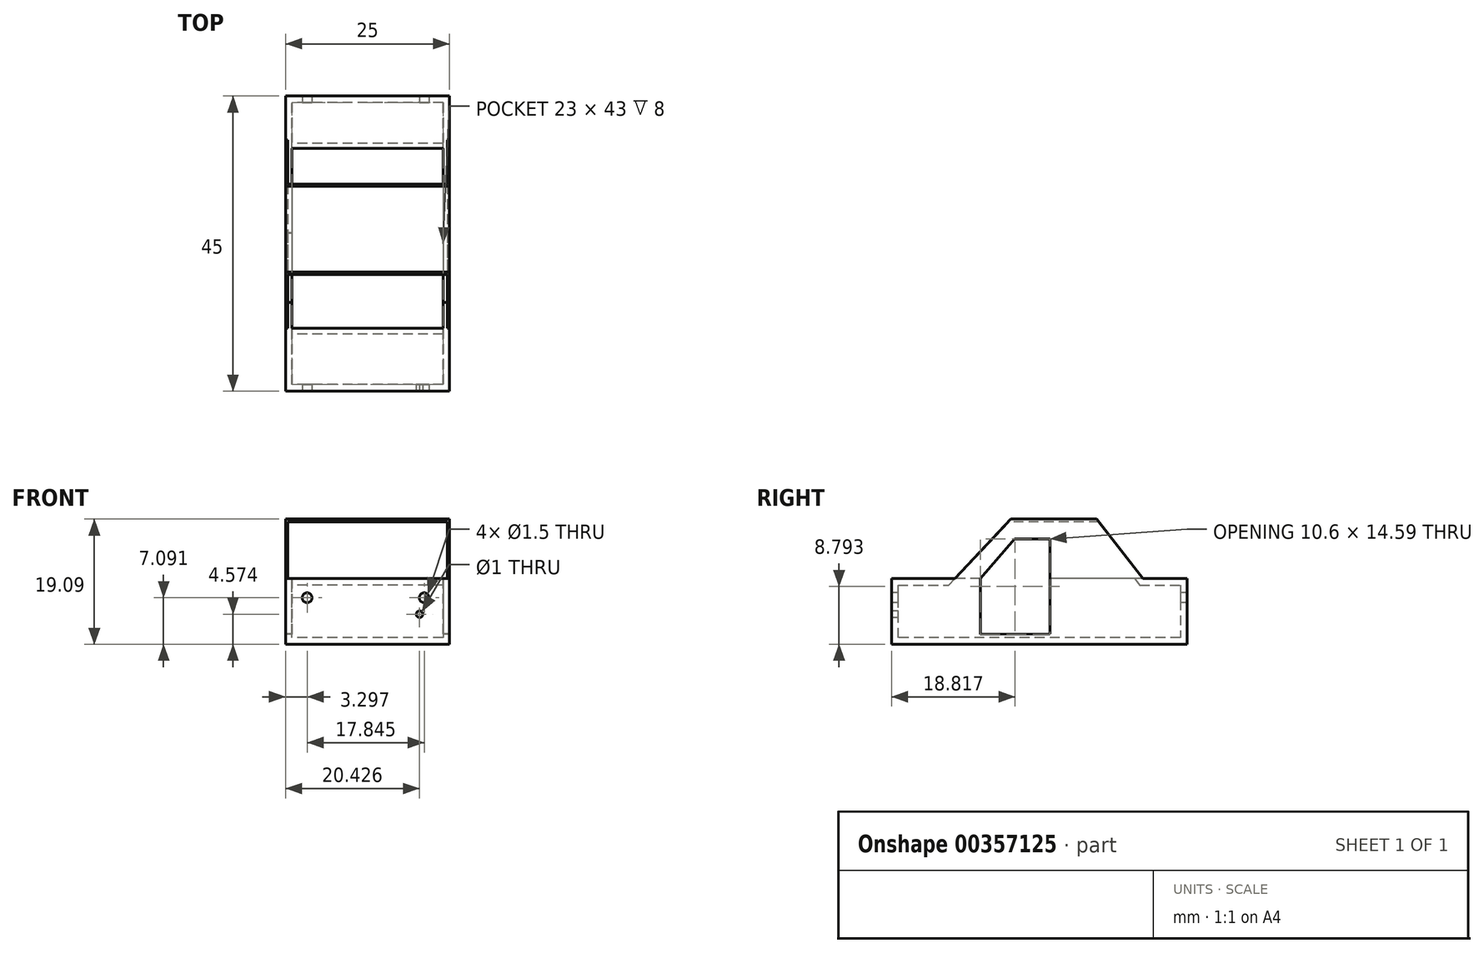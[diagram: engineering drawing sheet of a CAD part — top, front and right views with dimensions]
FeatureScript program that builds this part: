
annotation { "Feature Type Name" : "Feature", "Feature Type Description" : "" }
export const myFeature = defineFeature(function(context is Context, id is Id, definition is map)
    precondition{}
    {
        {
            var Q0;
            Q0=qCreatedBy(makeId("Right.planeOp"),FACE);
            var sketch = newSketch(context, id + "F0", { "sketchPlane" : qUnion([Q0])});
            skLineSegment(sketch, "E0", {"start": v(0, 0) * mm, "end": v(9.63, 0) * mm});
            skLineSegment(sketch, "E1", {"start": v(9.63, 0) * mm, "end": v(18.17, 9.09) * mm});
            skLineSegment(sketch, "E2", {"start": v(18.17, 9.09) * mm, "end": v(31.26, 9.09) * mm});
            skLineSegment(sketch, "E3", {"start": v(31.26, 9.09) * mm, "end": v(38.3, 0) * mm});
            skLineSegment(sketch, "E4", {"start": v(38.3, 0) * mm, "end": v(45, 0) * mm});
            skLineSegment(sketch, "E5", {"start": v(45, 0) * mm, "end": v(45, -10) * mm});
            skLineSegment(sketch, "E6", {"start": v(45, -10) * mm, "end": v(0, -10) * mm});
            skLineSegment(sketch, "E7", {"start": v(0, -10) * mm, "end": v(0, 0) * mm});
            skSolve(sketch);
        }
        {
            var Q0;
            Q0 = qSketchRegion(id + "F0", true);
            extrude(context, id + "F1", {"entities" : qUnion([Q0]), "depth" : 25 * mm});
        }
        {
            var Q0;
            Q0=makeQuery(id+"F1.opExtrude","SWEPT_FACE",FACE,{"disambiguationData":[OSD([sQuery(id+"F0.wireOp",EDGE,"E1")])]});
            shell(context, id + "F2", {"entities" : qUnion([Q0]), "thickness" : 1 * mm});
        }
        {
            var Q0;
            Q0=qCreatedBy(makeId("Right.planeOp"),FACE);
            var sketch = newSketch(context, id + "F3", { "sketchPlane" : qUnion([Q0])});
            skLineSegment(sketch, "E8", {"start": v(13.52, -8.5) * mm, "end": v(13.52, 0) * mm});
            skLineSegment(sketch, "E9", {"start": v(24.12, 6.09) * mm, "end": v(24.12, -8.41) * mm});
            skLineSegment(sketch, "E10", {"start": v(13.52, -8.5) * mm, "end": v(24.12, -8.41) * mm});
            skLineSegment(sketch, "E11", {"start": v(24.12, 6.09) * mm, "end": v(18.7, 6.09) * mm});
            skLineSegment(sketch, "E12", {"start": v(18.7, 6.09) * mm, "end": v(13.52, 0) * mm});
            skSolve(sketch);
        }
        {
            var Q0;
            Q0 = qSketchRegion(id + "F3", true);
            extrude(context, id + "F4", {"entities" : qUnion([Q0]), "operationType" : NewBodyOperationType.REMOVE, "depth" : 127 * mm});
        }
        {
            var Q0;
            Q0=qCreatedBy(makeId("Front.planeOp"),FACE);
            var sketch = newSketch(context, id + "F5", { "sketchPlane" : qUnion([Q0])});
            skLineSegment(sketch, "E13.bottom", {"start": v(24.67, 0) * mm, "end": v(0.34, 0) * mm});
            skLineSegment(sketch, "E13.top", {"start": v(24.67, 8.68) * mm, "end": v(0.34, 8.68) * mm});
            skLineSegment(sketch, "E13.left", {"start": v(24.67, 0) * mm, "end": v(24.67, 8.68) * mm});
            skLineSegment(sketch, "E13.right", {"start": v(0.34, 0) * mm, "end": v(0.34, 8.68) * mm});
            skSolve(sketch);
        }
        {
            var Q0;
            Q0 = qSketchRegion(id + "F5", true);
            extrude(context, id + "F6", {"entities" : qUnion([Q0]), "operationType" : NewBodyOperationType.REMOVE, "oppositeDirection" : true, "depth" : 82 * mm});
        }
        {
            var Q0;
            Q0=qCreatedBy(makeId("Front.planeOp"),FACE);
            var sketch = newSketch(context, id + "F7", { "sketchPlane" : qUnion([Q0])});
            skCircle(sketch, "E14", {"center": v(3.3, -2.9) * mm, "radius": 2.06 * mm});
            skCircle(sketch, "E15", {"center": v(21.14, -2.9) * mm, "radius": 2.21 * mm});
            skSolve(sketch);
        }
        {
            var Q0;
            Q0=sQuery(id+"F7.wireOp",VERTEX,"E14.center");
            var Q1;
            Q1=sQuery(id+"F7.wireOp",VERTEX,"E15.center");
            var Q2;
            Q2=makeQuery(id+"F1.opExtrude","SWEPT_BODY",BODY,{"disambiguationData":[OSD([sQuery(id+"F0.wireOp",EDGE,"E0"),sQuery(id+"F0.wireOp",EDGE,"E1"),sQuery(id+"F0.wireOp",EDGE,"E2"),sQuery(id+"F0.wireOp",EDGE,"E3"),sQuery(id+"F0.wireOp",EDGE,"E4"),sQuery(id+"F0.wireOp",EDGE,"E5"),sQuery(id+"F0.wireOp",EDGE,"E6"),sQuery(id+"F0.wireOp",EDGE,"E7")])]});
            hole(context, id + "F8", {"style" : HoleStyle.SIMPLE, "endStyle" : HoleEndStyle.THROUGH, "holeDiameter" : 1.5 * mm, "isTappedThrough" : true, "tappedDepth" : 12 * mm, "tapClearance" : 3, "locations" : qUnion([Q0, Q1]), "scope" : qUnion([Q2])});
        }
        {
            var Q0;
            Q0=qCreatedBy(makeId("Front.planeOp"),FACE);
            var sketch = newSketch(context, id + "F9", { "sketchPlane" : qUnion([Q0])});
            skCircle(sketch, "E16", {"center": v(20.43, -5.43) * mm, "radius": 0.5 * mm});
            skSolve(sketch);
        }
        {
            var Q0;
            Q0 = qSketchRegion(id + "F9", true);
            extrude(context, id + "F10", {"entities" : qUnion([Q0]), "operationType" : NewBodyOperationType.REMOVE, "oppositeDirection" : true, "depth" : 4.56 * mm});
        }
    });
